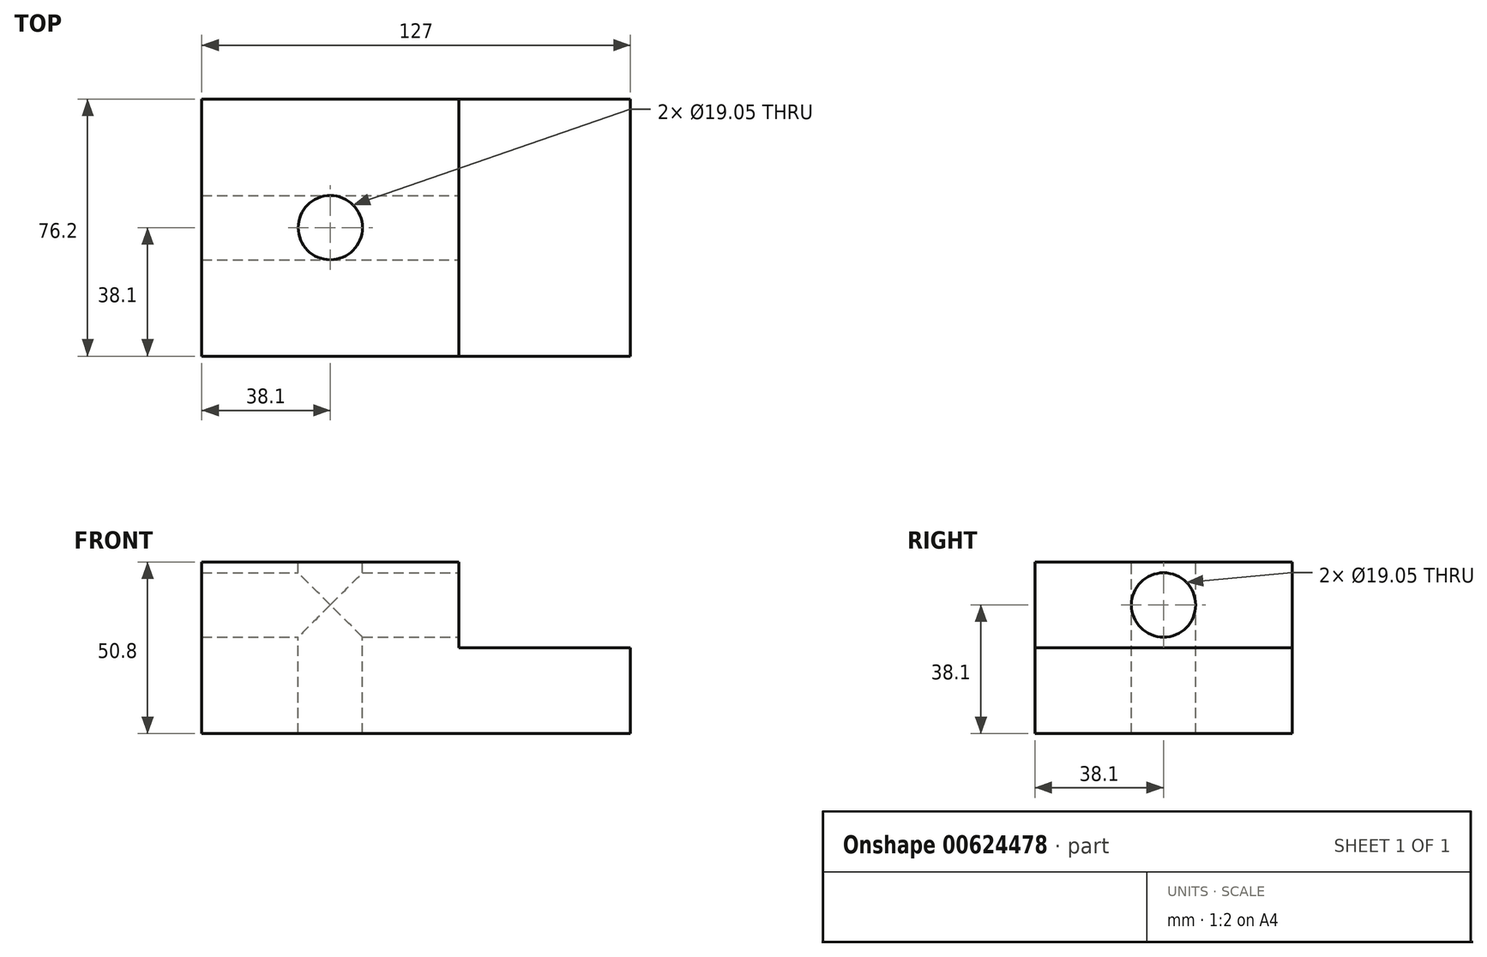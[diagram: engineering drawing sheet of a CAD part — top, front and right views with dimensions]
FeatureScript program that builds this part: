
annotation { "Feature Type Name" : "Feature", "Feature Type Description" : "" }
export const myFeature = defineFeature(function(context is Context, id is Id, definition is map)
    precondition{}
    {
        {
            var Q0;
            Q0=qCreatedBy(makeId("Front.planeOp"),FACE);
            var sketch = newSketch(context, id + "F0", { "sketchPlane" : qUnion([Q0])});
            skLineSegment(sketch, "E0.bottom", {"start": v(0, 0) * mm, "end": v(127, 0) * mm});
            skLineSegment(sketch, "E0.top", {"start": v(0, 50.8) * mm, "end": v(127, 50.8) * mm});
            skLineSegment(sketch, "E0.left", {"start": v(0, 0) * mm, "end": v(0, 50.8) * mm});
            skLineSegment(sketch, "E0.right", {"start": v(127, 0) * mm, "end": v(127, 50.8) * mm});
            skLineSegment(sketch, "E1", {"start": v(127, 25.4) * mm, "end": v(76.2, 25.4) * mm});
            skPoint(sketch, "E1.endSnap0", {"position": v(127, 25.4) * mm});
            skLineSegment(sketch, "E2", {"start": v(76.2, 25.4) * mm, "end": v(76.2, 50.8) * mm});
            skSolve(sketch);
        }
        {
            var Q0;
            {var subQ1=sQuery(id+"F0.wireOp",EDGE,"E0.bottom");Q0=makeQuery(id+"F0.imprint","IMPRINT",FACE,{"disambiguationData":[TD([[makeQuery(id+"F0.imprint","IMPRINT",EDGE,{"derivedFrom":subQ1}),1.0]])]});}
            extrude(context, id + "F1", {"entities" : qUnion([Q0]), "depth" : 76.2 * mm, "offsetDistance" : 25.4 * mm});
        }
        {
            var Q0;
            Q0=makeQuery(id+"F1.opExtrude","SWEPT_FACE",FACE,{"disambiguationData":[OSD([sQuery(id+"F0.wireOp",EDGE,"E2")])]});
            var sketch = newSketch(context, id + "F2", { "sketchPlane" : qUnion([Q0])});
            skPoint(sketch, "E3", {"position": v(-38.1, 38.1) * mm});
            skPoint(sketch, "E3.positionSnap0", {"position": v(-38.1, 50.8) * mm});
            skPoint(sketch, "E3.positionSnap1", {"position": v(0, 38.1) * mm});
            skSolve(sketch);
        }
        {
            var Q0;
            Q0=sQuery(id+"F2.wireOp",VERTEX,"E3");
            var Q1;
            Q1=makeQuery(id+"F1.opExtrude","SWEPT_BODY",BODY,{"disambiguationData":[OSD([sQuery(id+"F0.wireOp",EDGE,"E0.bottom"),sQuery(id+"F0.wireOp",EDGE,"E0.top"),sQuery(id+"F0.wireOp",EDGE,"E0.left"),sQuery(id+"F0.wireOp",EDGE,"E0.right"),sQuery(id+"F0.wireOp",EDGE,"E1"),sQuery(id+"F0.wireOp",EDGE,"E2")])]});
            hole(context, id + "F3", {"style" : HoleStyle.SIMPLE, "endStyle" : HoleEndStyle.THROUGH, "holeDiameter" : 19.05 * mm, "majorDiameter" : 6.35 * mm, "isTappedThrough" : true, "tappedDepth" : 12.7 * mm, "tapClearance" : 3, "locations" : qUnion([Q0]), "scope" : qUnion([Q1])});
        }
        {
            var Q0;
            Q0=makeQuery(id+"F1.opExtrude","SWEPT_FACE",FACE,{"disambiguationData":[OSD([sQuery(id+"F0.wireOp",EDGE,"E0.top")])]});
            var sketch = newSketch(context, id + "F4", { "sketchPlane" : qUnion([Q0])});
            skPoint(sketch, "E4", {"position": v(38.1, -38.1) * mm});
            skPoint(sketch, "E4.positionSnap0", {"position": v(38.1, 0) * mm});
            skPoint(sketch, "E4.positionSnap1", {"position": v(0, -38.1) * mm});
            skSolve(sketch);
        }
        {
            var Q0;
            Q0=sQuery(id+"F4.wireOp",VERTEX,"E4");
            var Q1;
            Q1=makeQuery(id+"F1.opExtrude","SWEPT_BODY",BODY,{"disambiguationData":[OSD([sQuery(id+"F0.wireOp",EDGE,"E0.bottom"),sQuery(id+"F0.wireOp",EDGE,"E0.top"),sQuery(id+"F0.wireOp",EDGE,"E0.left"),sQuery(id+"F0.wireOp",EDGE,"E0.right"),sQuery(id+"F0.wireOp",EDGE,"E1"),sQuery(id+"F0.wireOp",EDGE,"E2")])]});
            hole(context, id + "F5", {"style" : HoleStyle.SIMPLE, "endStyle" : HoleEndStyle.THROUGH, "holeDiameter" : 19.05 * mm, "majorDiameter" : 6.35 * mm, "isTappedThrough" : true, "tappedDepth" : 12.7 * mm, "tapClearance" : 3, "locations" : qUnion([Q0]), "scope" : qUnion([Q1])});
        }
    });
